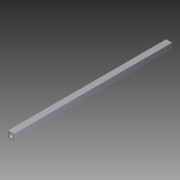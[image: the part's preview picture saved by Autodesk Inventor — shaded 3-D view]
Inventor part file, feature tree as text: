
AUTODESK INVENTOR PART (.ipt)
format: ipt  version: 2012 (Build 160160000, 160)  size: 76,288 bytes
history: native  units: in
note: dims shown in document units (in); Inventor stores cm internally (conversion verified against a paired STEP export)
features: extrude x1, sketch x1
ambient origin geometry x8: Origin, YZ Plane, XZ Plane, XY Plane, X Axis, Y Axis, Z Axis, Center Point
bodies: Solid1 (feature_tree)
feature tree (2):
  extrude  "Extrusion1"  Depth=0.125in
  sketch  "Sketch1"  dims[d0=0.125in d1=0.125in d2=0.125in d3=0.125in d4=1.0in d5=1.0in d6=27.0in d7=0.0in]
